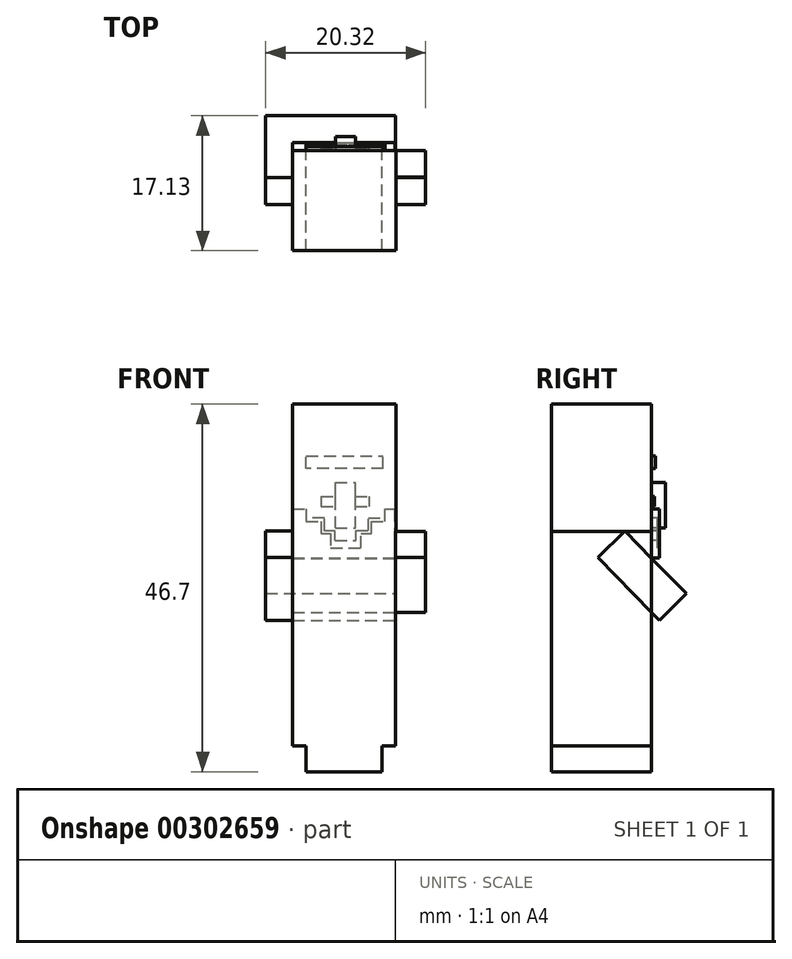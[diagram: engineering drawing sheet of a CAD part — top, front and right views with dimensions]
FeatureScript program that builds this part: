
annotation { "Feature Type Name" : "Feature", "Feature Type Description" : "" }
export const myFeature = defineFeature(function(context is Context, id is Id, definition is map)
    precondition{}
    {
        {
            var Q0;
            Q0=qCreatedBy(makeId("Front.planeOp"),FACE);
            var sketch = newSketch(context, id + "F0", { "sketchPlane" : qUnion([Q0])});
            skLineSegment(sketch, "E0.bottom", {"start": v(0, 0) * mm, "end": v(9.65, 0) * mm});
            skLineSegment(sketch, "E0.top", {"start": v(0, 3.25) * mm, "end": v(9.65, 3.25) * mm});
            skLineSegment(sketch, "E0.left", {"start": v(0, 0) * mm, "end": v(0, 3.25) * mm});
            skLineSegment(sketch, "E0.right", {"start": v(9.65, 0) * mm, "end": v(9.65, 3.25) * mm});
            skLineSegment(sketch, "E1", {"start": v(9.65, 3.25) * mm, "end": v(11.38, 3.25) * mm});
            skLineSegment(sketch, "E2.bottom", {"start": v(11.38, 3.25) * mm, "end": v(-1.7, 3.25) * mm});
            skLineSegment(sketch, "E2.left", {"start": v(11.38, 3.25) * mm, "end": v(11.38, 30.51) * mm});
            skLineSegment(sketch, "E2.right", {"start": v(-1.7, 3.25) * mm, "end": v(-1.7, 30.51) * mm});
            skLineSegment(sketch, "E3.bottom", {"start": v(11.38, 30.51) * mm, "end": v(11.4, 30.51) * mm});
            skLineSegment(sketch, "E3.top", {"start": v(-1.7, 46.7) * mm, "end": v(11.4, 46.7) * mm});
            skLineSegment(sketch, "E3.left", {"start": v(-1.7, 30.51) * mm, "end": v(-1.7, 46.7) * mm});
            skLineSegment(sketch, "E3.right", {"start": v(11.4, 30.51) * mm, "end": v(11.4, 46.7) * mm});
            skLineSegment(sketch, "E4", {"start": v(11.4, 30.51) * mm, "end": v(11.38, 30.51) * mm});
            skPoint(sketch, "E5.end.orphan", {"position": v(0, 29.4) * mm});
            skPoint(sketch, "E5.start.orphan", {"position": v(0, 30.51) * mm});
            skPoint(sketch, "E6.end.orphan", {"position": v(8.18, 28.23) * mm});
            skPoint(sketch, "E7.start.orphan", {"position": v(9.7, 29.4) * mm});
            skPoint(sketch, "E8.endSnap0", {"position": v(7.04, 29.29) * mm});
            skPoint(sketch, "E9.end.orphan", {"position": v(11.4, 31.76) * mm});
            skPoint(sketch, "E10.start.orphan", {"position": v(8.74, 31.76) * mm});
            skPoint(sketch, "E11.end.orphan", {"position": v(8.74, 30.35) * mm});
            skPoint(sketch, "E12.end.orphan", {"position": v(6.97, 30.9) * mm});
            skPoint(sketch, "E13.orphan", {"position": v(7.04, 30.35) * mm});
            skPoint(sketch, "E14.start.orphan", {"position": v(1.92, 30.26) * mm});
            skPoint(sketch, "E15.start.orphan", {"position": v(3.1, 30.9) * mm});
            skPoint(sketch, "E16.orphan", {"position": v(3.05, 30.26) * mm});
            skPoint(sketch, "E17.orphan", {"position": v(1.92, 31.76) * mm});
            skPoint(sketch, "E18.start.orphan", {"position": v(0, 31.76) * mm});
            skPoint(sketch, "E19.orphan", {"position": v(7.04, 28.23) * mm});
            skPoint(sketch, "E20.trimOffspring.end.orphan", {"position": v(7.04, 29.73) * mm});
            skPoint(sketch, "E21.orphan", {"position": v(11.38, 28.23) * mm});
            skSolve(sketch);
        }
        {
            var Q0;
            {var subQ5=sQuery(id+"F0.wireOp",EDGE,"E3.top");Q0=makeQuery(id+"F0.imprint","IMPRINT",FACE,{"disambiguationData":[TD([[makeQuery(id+"F0.imprint","IMPRINT",EDGE,{"derivedFrom":subQ5}),-1.0]])]});}
            var sketch = newSketch(context, id + "F1", { "sketchPlane" : qUnion([Q0])});
            skLineSegment(sketch, "E22.bottom", {"start": v(3.71, 30.94) * mm, "end": v(6.26, 30.94) * mm});
            skLineSegment(sketch, "E22.top", {"start": v(3.71, 36.77) * mm, "end": v(6.26, 36.77) * mm});
            skLineSegment(sketch, "E22.left", {"start": v(3.71, 30.94) * mm, "end": v(3.71, 36.77) * mm});
            skLineSegment(sketch, "E22.right", {"start": v(6.26, 30.94) * mm, "end": v(6.26, 36.77) * mm});
            skLineSegment(sketch, "E23.bottom", {"start": v(3.71, 36.77) * mm, "end": v(0, 36.77) * mm});
            skLineSegment(sketch, "E23.top", {"start": v(3.71, 38.51) * mm, "end": v(0, 38.51) * mm});
            skLineSegment(sketch, "E23.left", {"start": v(3.71, 36.77) * mm, "end": v(3.71, 38.51) * mm});
            skLineSegment(sketch, "E23.right", {"start": v(0, 36.77) * mm, "end": v(0, 38.51) * mm});
            skPoint(sketch, "E24.oppositeSnap0", {"position": v(1.86, 38.51) * mm});
            skLineSegment(sketch, "E24.bottom", {"start": v(6.26, 36.77) * mm, "end": v(9.8, 36.77) * mm});
            skLineSegment(sketch, "E24.top", {"start": v(6.26, 38.51) * mm, "end": v(9.8, 38.51) * mm});
            skLineSegment(sketch, "E24.left", {"start": v(6.26, 36.77) * mm, "end": v(6.26, 38.51) * mm});
            skLineSegment(sketch, "E24.right", {"start": v(9.8, 36.77) * mm, "end": v(9.8, 38.51) * mm});
            skLineSegment(sketch, "E25.bottom", {"start": v(0, 38.51) * mm, "end": v(9.8, 38.51) * mm});
            skLineSegment(sketch, "E25.top", {"start": v(0, 40.12) * mm, "end": v(9.8, 40.12) * mm});
            skLineSegment(sketch, "E25.left", {"start": v(0, 38.51) * mm, "end": v(0, 40.12) * mm});
            skLineSegment(sketch, "E25.right", {"start": v(9.8, 38.51) * mm, "end": v(9.8, 40.12) * mm});
            skLineSegment(sketch, "E26", {"start": v(1.86, 38.51) * mm, "end": v(1.86, 36.77) * mm});
            skLineSegment(sketch, "E27", {"start": v(1.86, 36.77) * mm, "end": v(1.86, 38.51) * mm});
            skLineSegment(sketch, "E28", {"start": v(8.02, 38.51) * mm, "end": v(8.02, 36.77) * mm});
            skLineSegment(sketch, "E29.bottom", {"start": v(1.91, 34.97) * mm, "end": v(3.71, 34.97) * mm});
            skLineSegment(sketch, "E29.top", {"start": v(1.91, 33.67) * mm, "end": v(3.71, 33.67) * mm});
            skLineSegment(sketch, "E29.left", {"start": v(1.91, 34.97) * mm, "end": v(1.91, 33.67) * mm});
            skLineSegment(sketch, "E29.right", {"start": v(8.02, 34.97) * mm, "end": v(8.02, 33.67) * mm});
            skLineSegment(sketch, "E30.trimOffspring", {"start": v(6.26, 34.97) * mm, "end": v(8.02, 34.97) * mm});
            skLineSegment(sketch, "E31.trimOffspring", {"start": v(6.26, 33.67) * mm, "end": v(8.02, 33.67) * mm});
            skPoint(sketch, "E32.oppositeSnap0", {"position": v(-0.84, 33.36) * mm});
            skPoint(sketch, "E33.orphan", {"position": v(0, 33.36) * mm});
            skPoint(sketch, "E34.top.end.orphan", {"position": v(-1.69, 33.36) * mm});
            skPoint(sketch, "E32.right.end.orphan", {"position": v(11.4, 33.36) * mm});
            skSolve(sketch);
        }
        {
            var Q0;
            Q0 = qSketchRegion(id + "F0", true);
            extrude(context, id + "F2", {"entities" : qUnion([Q0]), "depth" : 12.7 * mm});
        }
        {
            var Q0;
            Q0=makeQuery(id+"F2.opExtrude","SWEPT_FACE",FACE,{"disambiguationData":[OSD([sQuery(id+"F0.wireOp",EDGE,"E2.left")])]});
            var sketch = newSketch(context, id + "F3", { "sketchPlane" : qUnion([Q0])});
            skSolve(sketch);
        }
        {
            var Q0;
            {var subQ3=sQuery(id+"F1.wireOp",EDGE,"E22.bottom");Q0=makeQuery(id+"F1.imprint","IMPRINT",FACE,{"disambiguationData":[TD([[makeQuery(id+"F1.imprint","IMPRINT",EDGE,{"derivedFrom":subQ3}),1.0]])]});}
            extrude(context, id + "F4", {"entities" : qUnion([Q0]), "operationType" : NewBodyOperationType.ADD, "oppositeDirection" : true, "depth" : 1.78 * mm});
        }
        {
            var Q0;
            Q0=makeQuery(id+"F1.imprint","IMPRINT",FACE,{"disambiguationData":[TD([[makeQuery(id+"F1.imprint","IMPRINT",EDGE,{"derivedFrom":sQuery(id+"F1.wireOp",EDGE,"E25.top")}),-1.0]])]});
            extrude(context, id + "F5", {"entities" : qUnion([Q0]), "operationType" : NewBodyOperationType.ADD, "oppositeDirection" : true, "depth" : 0.5 * mm});
        }
        {
            var Q0;
            {var subQ0=sQuery(id+"F1.wireOp",EDGE,"E29.bottom");Q0=makeQuery(id+"F1.imprint","IMPRINT",FACE,{"disambiguationData":[TD([[makeQuery(id+"F1.imprint","IMPRINT",EDGE,{"derivedFrom":subQ0}),-1.0]])]});}
            extrude(context, id + "F6", {"entities" : qUnion([Q0]), "operationType" : NewBodyOperationType.ADD, "oppositeDirection" : true, "depth" : 0.38 * mm});
        }
        {
            var Q0;
            Q0=makeQuery(id+"F1.imprint","IMPRINT",FACE,{"disambiguationData":[TD([[makeQuery(id+"F1.imprint","IMPRINT",EDGE,{"derivedFrom":sQuery(id+"F1.wireOp",EDGE,"E29.right")}),-1.0]])]});
            extrude(context, id + "F7", {"entities" : qUnion([Q0]), "operationType" : NewBodyOperationType.ADD, "oppositeDirection" : true, "depth" : 0.38 * mm});
        }
        {
            var Q0;
            {var subQ0=sQuery(id+"F0.wireOp",EDGE,"E2.left");Q0=makeQuery(id+"F3.imprint","IMPRINT",FACE,{"disambiguationData":[TD([[makeQuery(id+"F3.imprint","IMPRINT",EDGE,{"derivedFrom":makeQuery(id+"F2.opExtrude","CAP_EDGE",EDGE,{"disambiguationData":[OSD([subQ0])],"isStart":true})}),1.0]])]});}
            var sketch = newSketch(context, id + "F8", { "sketchPlane" : qUnion([Q0])});
            skLineSegment(sketch, "E35", {"start": v(-3.4, 30.57) * mm, "end": v(4.43, 22.62) * mm});
            skLineSegment(sketch, "E36", {"start": v(4.43, 22.62) * mm, "end": v(-3.4, 30.57) * mm});
            skLineSegment(sketch, "E37", {"start": v(-3.4, 30.57) * mm, "end": v(-6.82, 27.2) * mm});
            skLineSegment(sketch, "E38", {"start": v(4.43, 22.62) * mm, "end": v(1, 19.25) * mm});
            skLineSegment(sketch, "E39", {"start": v(1, 19.25) * mm, "end": v(4.43, 22.62) * mm});
            skLineSegment(sketch, "E40", {"start": v(-6.82, 27.2) * mm, "end": v(1, 19.25) * mm});
            skSolve(sketch);
        }
        {
            var Q0;
            {var subQ4=sQuery(id+"F8.wireOp",EDGE,"E37");var subQ8=sQuery(id+"F8.wireOp",EDGE,"E40");var subQ9=makeQuery(id+"F8.imprint","INTERSECT",VERTEX,{"derivedFrom":[subQ4,subQ8]});Q0=makeQuery(id+"F8.imprint","IMPRINT",FACE,{"disambiguationData":[TD([[makeQuery(id+"F8.imprint","IMPRINT",EDGE,{"disambiguationData":[TD([[subQ9,-1.0]])],"derivedFrom":subQ8}),1.0]])]});}
            var Q1;
            {var subQ0=sQuery(id+"F8.wireOp",EDGE,"E39");Q1=makeQuery(id+"F8.imprint","IMPRINT",FACE,{"disambiguationData":[TD([[makeQuery(id+"F8.imprint","IMPRINT",EDGE,{"derivedFrom":subQ0}),1.0]])]});}
            extrude(context, id + "F9", {"entities" : qUnion([Q0, Q1]), "operationType" : NewBodyOperationType.ADD, "depth" : 3.8 * mm});
        }
        {
            var Q0;
            Q0 = qSketchRegion(id + "F8", true);
            extrude(context, id + "F10", {"entities" : qUnion([Q0]), "operationType" : NewBodyOperationType.ADD, "oppositeDirection" : true, "depth" : 16.5 * mm});
        }
        {
            var Q0;
            {var subQ10=sQuery(id+"F1.wireOp",EDGE,"E22.bottom");Q0=makeQuery(id+"F1.imprint","IMPRINT",FACE,{"disambiguationData":[TD([[makeQuery(id+"F1.imprint","IMPRINT",EDGE,{"derivedFrom":subQ10}),-1.0]])]});}
            var sketch = newSketch(context, id + "F11", { "sketchPlane" : qUnion([Q0])});
            skLineSegment(sketch, "E41", {"start": v(-1.7, 33.36) * mm, "end": v(0, 33.36) * mm});
            skLineSegment(sketch, "E42", {"start": v(0, 33.36) * mm, "end": v(0, 31.78) * mm});
            skLineSegment(sketch, "E43", {"start": v(0, 31.78) * mm, "end": v(1.9, 31.78) * mm});
            skLineSegment(sketch, "E44", {"start": v(1.9, 31.78) * mm, "end": v(1.9, 30.27) * mm});
            skLineSegment(sketch, "E45", {"start": v(1.9, 30.27) * mm, "end": v(3.1, 30.27) * mm});
            skLineSegment(sketch, "E46", {"start": v(3.1, 30.27) * mm, "end": v(3.1, 28.43) * mm});
            skLineSegment(sketch, "E47", {"start": v(3.1, 28.43) * mm, "end": v(6.97, 28.43) * mm});
            skLineSegment(sketch, "E48", {"start": v(6.97, 28.43) * mm, "end": v(6.97, 30.27) * mm});
            skLineSegment(sketch, "E49", {"start": v(6.97, 30.27) * mm, "end": v(8.3, 30.27) * mm});
            skLineSegment(sketch, "E50", {"start": v(8.3, 30.27) * mm, "end": v(8.3, 31.78) * mm});
            skLineSegment(sketch, "E51", {"start": v(8.3, 31.78) * mm, "end": v(10.01, 31.78) * mm});
            skLineSegment(sketch, "E52", {"start": v(10.01, 31.78) * mm, "end": v(10.01, 33.36) * mm});
            skLineSegment(sketch, "E53", {"start": v(10.01, 33.36) * mm, "end": v(11.32, 33.36) * mm});
            skLineSegment(sketch, "E54", {"start": v(11.32, 33.36) * mm, "end": v(10.01, 33.36) * mm});
            skLineSegment(sketch, "E55", {"start": v(3.67, 29.36) * mm, "end": v(6.34, 29.36) * mm});
            skLineSegment(sketch, "E56", {"start": v(6.34, 29.36) * mm, "end": v(6.34, 30.64) * mm});
            skLineSegment(sketch, "E57", {"start": v(6.34, 30.64) * mm, "end": v(7.9, 30.64) * mm});
            skLineSegment(sketch, "E58", {"start": v(7.9, 30.64) * mm, "end": v(7.9, 32.27) * mm});
            skLineSegment(sketch, "E59", {"start": v(7.9, 32.27) * mm, "end": v(10.01, 32.27) * mm});
            skLineSegment(sketch, "E60", {"start": v(10.01, 32.27) * mm, "end": v(7.9, 32.27) * mm});
            skLineSegment(sketch, "E61", {"start": v(3.67, 29.36) * mm, "end": v(3.67, 30.62) * mm});
            skLineSegment(sketch, "E62", {"start": v(3.67, 30.62) * mm, "end": v(2.34, 30.62) * mm});
            skLineSegment(sketch, "E63", {"start": v(2.34, 30.62) * mm, "end": v(2.34, 32.27) * mm});
            skLineSegment(sketch, "E64", {"start": v(2.34, 32.27) * mm, "end": v(0, 32.27) * mm});
            skLineSegment(sketch, "E65", {"start": v(-1.7, 33.36) * mm, "end": v(-1.7, 27.17) * mm});
            skLineSegment(sketch, "E66", {"start": v(-1.7, 27.17) * mm, "end": v(11.32, 27.17) * mm});
            skLineSegment(sketch, "E67", {"start": v(11.32, 27.17) * mm, "end": v(11.32, 33.36) * mm});
            skSolve(sketch);
        }
        {
            var Q0;
            {var subQ7=sQuery(id+"F11.wireOp",EDGE,"E43");Q0=makeQuery(id+"F11.imprint","IMPRINT",FACE,{"disambiguationData":[TD([[makeQuery(id+"F11.imprint","IMPRINT",EDGE,{"derivedFrom":subQ7}),-1.0]])]});}
            extrude(context, id + "F12", {"entities" : qUnion([Q0]), "operationType" : NewBodyOperationType.ADD, "oppositeDirection" : true, "depth" : 1.02 * mm});
        }
        {
            var Q0;
            {var subQ1=sQuery(id+"F11.wireOp",EDGE,"E43");Q0=makeQuery(id+"F11.imprint","IMPRINT",FACE,{"disambiguationData":[TD([[makeQuery(id+"F11.imprint","IMPRINT",EDGE,{"derivedFrom":subQ1}),1.0]])]});}
            extrude(context, id + "F13", {"entities" : qUnion([Q0]), "operationType" : NewBodyOperationType.ADD, "oppositeDirection" : true, "depth" : 0.76 * mm});
        }
    });
